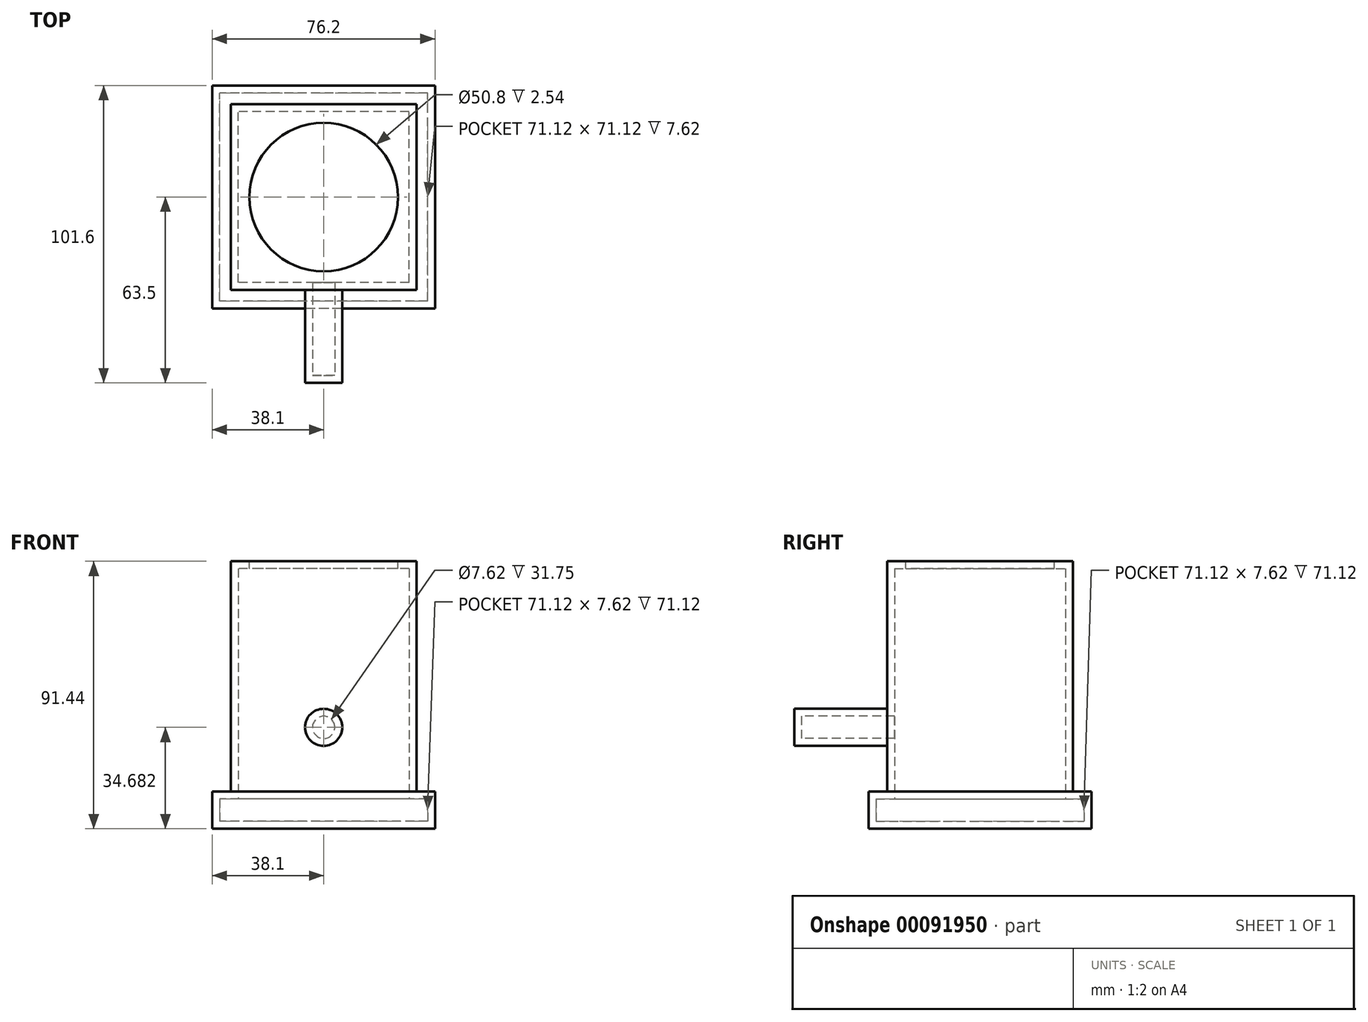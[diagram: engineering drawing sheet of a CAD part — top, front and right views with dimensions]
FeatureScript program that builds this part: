
annotation { "Feature Type Name" : "Feature", "Feature Type Description" : "" }
export const myFeature = defineFeature(function(context is Context, id is Id, definition is map)
    precondition{}
    {
        {
            var Q0;
            Q0=qCreatedBy(makeId("Top.planeOp"),FACE);
            var sketch = newSketch(context, id + "F0", { "sketchPlane" : qUnion([Q0])});
            skLineSegment(sketch, "E0.bottom", {"start": v(38.1, -38.1) * mm, "end": v(-38.1, -38.1) * mm});
            skLineSegment(sketch, "E0.top", {"start": v(38.1, 38.1) * mm, "end": v(-38.1, 38.1) * mm});
            skLineSegment(sketch, "E0.left", {"start": v(38.1, -38.1) * mm, "end": v(38.1, 38.1) * mm});
            skLineSegment(sketch, "E0.right", {"start": v(-38.1, -38.1) * mm, "end": v(-38.1, 38.1) * mm});
            skPoint(sketch, "E0.middle", {"position": v(0, 0) * mm});
            skSolve(sketch);
        }
        {
            var Q0;
            Q0 = qSketchRegion(id + "F0", true);
            extrude(context, id + "F1", {"entities" : qUnion([Q0]), "depth" : 12.7 * mm});
        }
        {
            var Q0;
            Q0=makeQuery(id+"F1.opExtrude","CAP_FACE",FACE,{"disambiguationData":[OSD([sQuery(id+"F0.wireOp",EDGE,"E0.bottom"),sQuery(id+"F0.wireOp",EDGE,"E0.top"),sQuery(id+"F0.wireOp",EDGE,"E0.left"),sQuery(id+"F0.wireOp",EDGE,"E0.right")])],"isStart":false});
            var sketch = newSketch(context, id + "F2", { "sketchPlane" : qUnion([Q0])});
            skLineSegment(sketch, "E1.bottom", {"start": v(31.75, -31.75) * mm, "end": v(-31.75, -31.75) * mm});
            skLineSegment(sketch, "E1.top", {"start": v(31.75, 31.75) * mm, "end": v(-31.75, 31.75) * mm});
            skLineSegment(sketch, "E1.left", {"start": v(31.75, -31.75) * mm, "end": v(31.75, 31.75) * mm});
            skLineSegment(sketch, "E1.right", {"start": v(-31.75, -31.75) * mm, "end": v(-31.75, 31.75) * mm});
            skPoint(sketch, "E1.middle", {"position": v(0, 0) * mm});
            skSolve(sketch);
        }
        {
            var Q0;
            Q0 = qSketchRegion(id + "F2", true);
            extrude(context, id + "F3", {"entities" : qUnion([Q0]), "operationType" : NewBodyOperationType.ADD, "depth" : 76.2 * mm});
        }
        {
            var Q0;
            Q0=makeQuery(id+"F3.opExtrude","SWEPT_FACE",FACE,{"disambiguationData":[OSD([sQuery(id+"F2.wireOp",EDGE,"E1.bottom")])]});
            var sketch = newSketch(context, id + "F4", { "sketchPlane" : qUnion([Q0])});
            skCircle(sketch, "E2", {"center": v(0, 34.68) * mm, "radius": 6.35 * mm});
            skSolve(sketch);
        }
        {
            var Q0;
            Q0=makeQuery(id+"F4.imprint","IMPRINT",FACE,{"disambiguationData":[TD([[makeQuery(id+"F4.imprint","IMPRINT",EDGE,{"derivedFrom":sQuery(id+"F4.wireOp",EDGE,"E2")}),1.0]])]});
            extrude(context, id + "F5", {"entities" : qUnion([Q0]), "operationType" : NewBodyOperationType.ADD, "endBound" : BoundingType.SYMMETRIC, "oppositeDirection" : true, "depth" : 63.5 * mm});
        }
        {
            var Q0;
            Q0=makeQuery(id+"F3.opExtrude","CAP_FACE",FACE,{"disambiguationData":[OSD([sQuery(id+"F2.wireOp",EDGE,"E1.bottom"),sQuery(id+"F2.wireOp",EDGE,"E1.top"),sQuery(id+"F2.wireOp",EDGE,"E1.left"),sQuery(id+"F2.wireOp",EDGE,"E1.right")])],"isStart":false});
            shell(context, id + "F6", {"entities" : qUnion([Q0]), "thickness" : 2.54 * mm});
        }
        {
            var Q0;
            Q0=makeQuery(id+"F3.opExtrude","CAP_FACE",FACE,{"disambiguationData":[OSD([sQuery(id+"F2.wireOp",EDGE,"E1.bottom"),sQuery(id+"F2.wireOp",EDGE,"E1.top"),sQuery(id+"F2.wireOp",EDGE,"E1.left"),sQuery(id+"F2.wireOp",EDGE,"E1.right")])],"isStart":false});
            var sketch = newSketch(context, id + "F7", { "sketchPlane" : qUnion([Q0])});
            skLineSegment(sketch, "E3.bottom", {"start": v(-31.75, 31.75) * mm, "end": v(31.75, 31.75) * mm});
            skLineSegment(sketch, "E3.top", {"start": v(-31.75, -31.75) * mm, "end": v(31.75, -31.75) * mm});
            skLineSegment(sketch, "E3.left", {"start": v(-31.75, 31.75) * mm, "end": v(-31.75, -31.75) * mm});
            skLineSegment(sketch, "E3.right", {"start": v(31.75, 31.75) * mm, "end": v(31.75, -31.75) * mm});
            skSolve(sketch);
        }
        {
            var Q0;
            Q0 = qSketchRegion(id + "F7", true);
            extrude(context, id + "F8", {"entities" : qUnion([Q0]), "operationType" : NewBodyOperationType.ADD, "depth" : 2.54 * mm});
        }
        {
            var Q0;
            Q0=makeQuery(id+"F8.opExtrude","CAP_FACE",FACE,{"disambiguationData":[OSD([sQuery(id+"F7.wireOp",EDGE,"E3.bottom"),sQuery(id+"F7.wireOp",EDGE,"E3.top"),sQuery(id+"F7.wireOp",EDGE,"E3.left"),sQuery(id+"F7.wireOp",EDGE,"E3.right")])],"isStart":false});
            var sketch = newSketch(context, id + "F9", { "sketchPlane" : qUnion([Q0])});
            skCircle(sketch, "E4", {"center": v(0, 0) * mm, "radius": 25.4 * mm});
            skSolve(sketch);
        }
        {
            var Q0;
            Q0=makeQuery(id+"F9.imprint","IMPRINT",FACE,{"disambiguationData":[TD([[makeQuery(id+"F9.imprint","IMPRINT",EDGE,{"derivedFrom":sQuery(id+"F9.wireOp",EDGE,"E4")}),1.0]])]});
            extrude(context, id + "F10", {"entities" : qUnion([Q0]), "operationType" : NewBodyOperationType.REMOVE, "oppositeDirection" : true, "depth" : 25.4 * mm});
        }
    });
